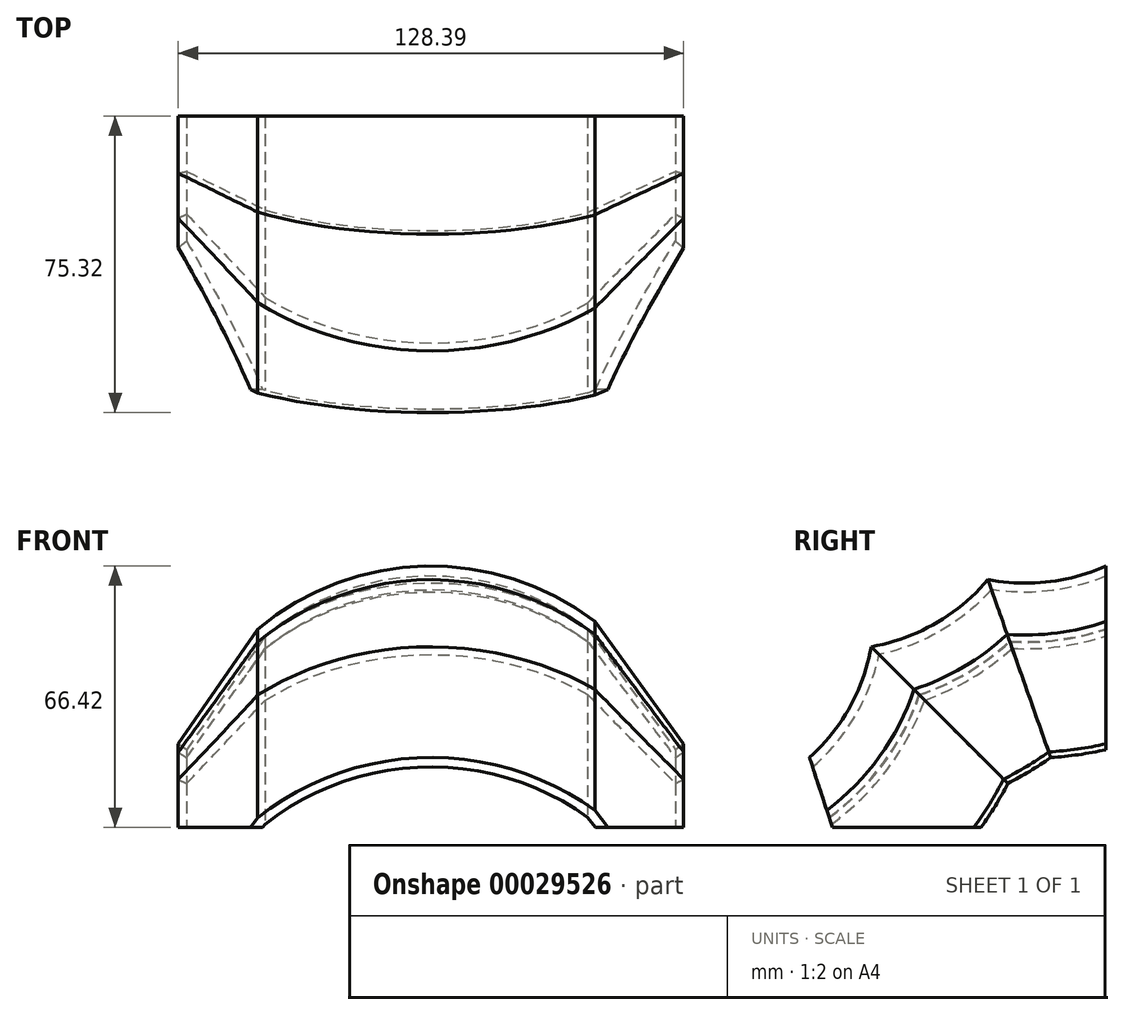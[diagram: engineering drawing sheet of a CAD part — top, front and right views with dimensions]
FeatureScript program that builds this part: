
annotation { "Feature Type Name" : "Feature", "Feature Type Description" : "" }
export const myFeature = defineFeature(function(context is Context, id is Id, definition is map)
    precondition{}
    {
        {
            var Q0;
            Q0=qCreatedBy(makeId("Front.planeOp"),FACE);
            var sketch = newSketch(context, id + "F0", { "sketchPlane" : qUnion([Q0])});
            skArc(sketch, "E0", {"start": v(37.8, 30.74) * mm, "mid": v(-3.49, 44.1) * mm, "end": v(-44.12, 28.86) * mm});
            skLineSegment(sketch, "E1", {"start": v(37.8, 30.74) * mm, "end": v(60.13, 0) * mm});
            skLineSegment(sketch, "E2", {"start": v(-44.12, 28.86) * mm, "end": v(-64.09, 0) * mm});
            skLineSegment(sketch, "E3.0", {"start": v(39.64, 32.53) * mm, "end": v(62.18, 1.5) * mm});
            skArc(sketch, "E3.1", {"start": v(39.64, 32.53) * mm, "mid": v(-3.53, 46.64) * mm, "end": v(-46.02, 30.58) * mm});
            skLineSegment(sketch, "E3.2", {"start": v(-46.02, 30.58) * mm, "end": v(-66.2, 1.4) * mm});
            skLineSegment(sketch, "E4", {"start": v(62.18, 1.5) * mm, "end": v(60.13, 0) * mm});
            skLineSegment(sketch, "E5", {"start": v(-64.09, 0) * mm, "end": v(-66.2, 1.4) * mm});
            skSolve(sketch);
        }
        {
            var Q0;
            Q0=qCreatedBy(makeId("Right.planeOp"),FACE);
            var sketch = newSketch(context, id + "F1", { "sketchPlane" : qUnion([Q0])});
            skLineSegment(sketch, "E6", {"start": v(0, 0) * mm, "end": v(0, 48.78) * mm});
            skLineSegment(sketch, "E7", {"start": v(0, 0) * mm, "end": v(-75.98, 0) * mm});
            skArc(sketch, "E8", {"start": v(-30.74, 45.3) * mm, "mid": v(-15.09, 44.54) * mm, "end": v(0, 48.78) * mm});
            skArc(sketch, "E9", {"start": v(-61.33, 27.82) * mm, "mid": v(-44.4, 33.71) * mm, "end": v(-30.74, 45.3) * mm});
            skArc(sketch, "E10", {"start": v(-75.98, 0) * mm, "mid": v(-66.3, 12.67) * mm, "end": v(-61.33, 27.82) * mm});
            skSolve(sketch);
        }
        {
            var Q0;
            Q0=makeQuery(id+"F0.imprint","IMPRINT",FACE,{"disambiguationData":[TD([[makeQuery(id+"F0.imprint","IMPRINT",EDGE,{"derivedFrom":sQuery(id+"F0.wireOp",EDGE,"E0")}),-1.0]])]});
            var Q1;
            Q1=sQuery(id+"F1.wireOp",EDGE,"E8");
            var Q2;
            Q2=sQuery(id+"F1.wireOp",EDGE,"E9");
            var Q3;
            Q3=sQuery(id+"F1.wireOp",EDGE,"E10");
            sweep(context, id + "F2", {"profiles" : qUnion([Q0]), "path" : qUnion([Q1, Q2, Q3])});
        }
        {
            var Q0;
            Q0=qCreatedBy(makeId("Front.planeOp"),FACE);
            var sketch = newSketch(context, id + "F3", { "sketchPlane" : qUnion([Q0])});
            skLineSegment(sketch, "E11", {"start": v(0, 0) * mm, "end": v(0, -19.76) * mm});
            skLineSegment(sketch, "E12", {"start": v(0, -19.76) * mm, "end": v(88.36, -19.76) * mm});
            skLineSegment(sketch, "E13", {"start": v(88.36, -19.76) * mm, "end": v(88.36, -107.78) * mm});
            skLineSegment(sketch, "E14", {"start": v(88.36, -107.78) * mm, "end": v(-112.39, -107.78) * mm});
            skLineSegment(sketch, "E15", {"start": v(-112.39, -107.78) * mm, "end": v(-112.39, -19.76) * mm});
            skLineSegment(sketch, "E16", {"start": v(-112.39, -19.76) * mm, "end": v(0, -19.76) * mm});
            skSolve(sketch);
        }
        {
            var Q0;
            Q0=makeQuery(id+"F3.imprint","IMPRINT",FACE,{"disambiguationData":[TD([[makeQuery(id+"F3.imprint","IMPRINT",EDGE,{"derivedFrom":sQuery(id+"F3.wireOp",EDGE,"E12")}),-1.0]])]});
            extrude(context, id + "F4", {"entities" : qUnion([Q0]), "operationType" : NewBodyOperationType.REMOVE, "depth" : 91.31 * mm});
        }
    });
